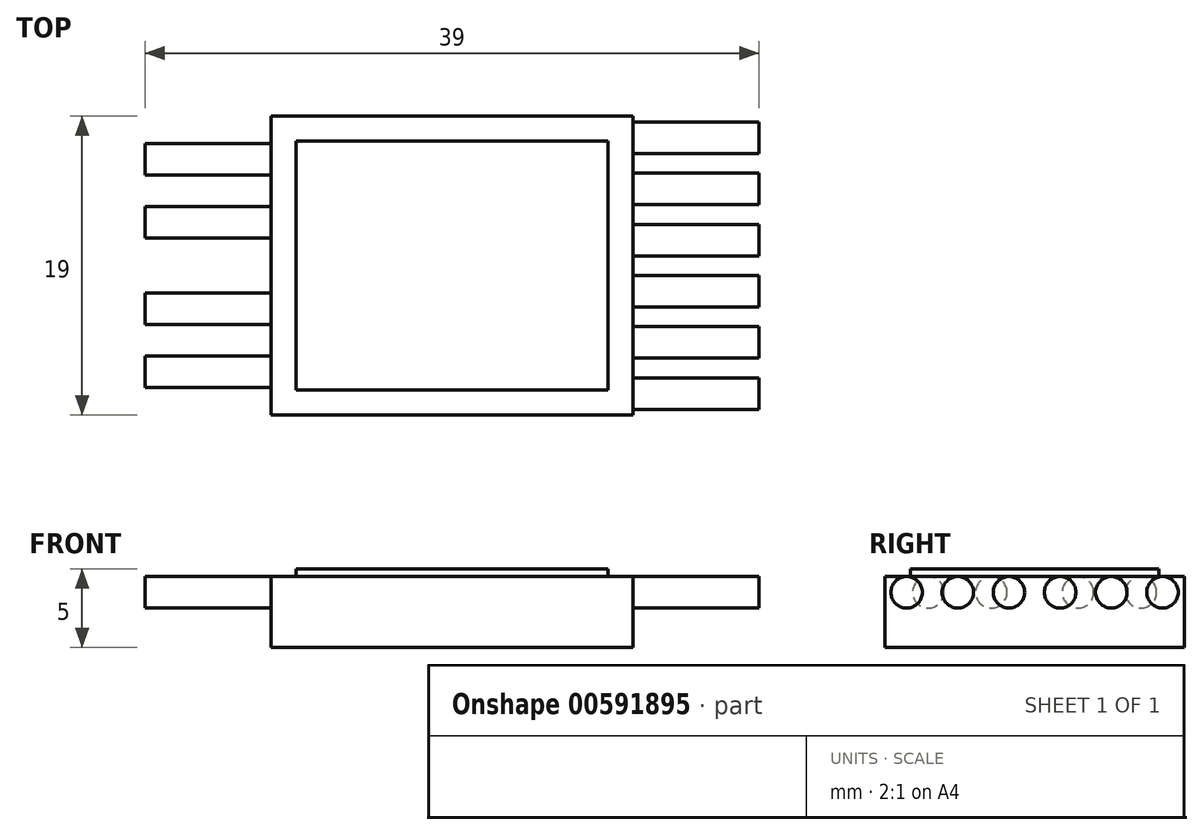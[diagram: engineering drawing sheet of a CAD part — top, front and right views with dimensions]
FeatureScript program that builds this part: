
annotation { "Feature Type Name" : "Feature", "Feature Type Description" : "" }
export const myFeature = defineFeature(function(context is Context, id is Id, definition is map)
    precondition{}
    {
        {
            var Q0;
            Q0=qCreatedBy(makeId("Top.planeOp"),FACE);
            var sketch = newSketch(context, id + "F0", { "sketchPlane" : qUnion([Q0])});
            skLineSegment(sketch, "E0.bottom", {"start": v(11.5, 9.5) * mm, "end": v(-11.5, 9.5) * mm});
            skLineSegment(sketch, "E0.top", {"start": v(11.5, -9.5) * mm, "end": v(-11.5, -9.5) * mm});
            skLineSegment(sketch, "E0.left", {"start": v(11.5, 9.5) * mm, "end": v(11.5, -9.5) * mm});
            skLineSegment(sketch, "E0.right", {"start": v(-11.5, 9.5) * mm, "end": v(-11.5, -9.5) * mm});
            skPoint(sketch, "E0.middle", {"position": v(0, 0) * mm});
            skSolve(sketch);
        }
        {
            var Q0;
            Q0 = qSketchRegion(id + "F0", true);
            extrude(context, id + "F1", {"entities" : qUnion([Q0]), "depth" : 5 * mm, "offsetDistance" : 25 * mm, "symmetric" : true});
        }
        {
            var Q0;
            Q0=makeQuery(id+"F1.opExtrude","SWEPT_FACE",FACE,{"disambiguationData":[OSD([sQuery(id+"F0.wireOp",EDGE,"E0.left")])]});
            var sketch = newSketch(context, id + "F2", { "sketchPlane" : qUnion([Q0])});
            skCircle(sketch, "E1", {"center": v(-8.13, 1) * mm, "radius": 1 * mm});
            skCircle(sketch, "E2.1.0.0", {"center": v(-4.88, 1) * mm, "radius": 1 * mm});
            skCircle(sketch, "E2.2.0.0", {"center": v(-1.63, 1) * mm, "radius": 1 * mm});
            skCircle(sketch, "E2.3.0.0", {"center": v(1.62, 1) * mm, "radius": 1 * mm});
            skCircle(sketch, "E2.4.0.0", {"center": v(4.87, 1) * mm, "radius": 1 * mm});
            skCircle(sketch, "E2.5.0.0", {"center": v(8.12, 1) * mm, "radius": 1 * mm});
            skLineSegment(sketch, "E2.direction1", {"start": v(-8.13, 1) * mm, "end": v(-4.88, 1) * mm, "construction": true});
            skLineSegment(sketch, "E3", {"start": v(-1.63, 1) * mm, "end": v(1.62, 1) * mm, "construction": true});
            skPoint(sketch, "E4", {"position": v(0, 1) * mm});
            skSolve(sketch);
        }
        {
            var Q0;
            Q0 = qSketchRegion(id + "F2", true);
            extrude(context, id + "F3", {"entities" : qUnion([Q0]), "operationType" : NewBodyOperationType.ADD, "depth" : 8 * mm, "offsetDistance" : 25 * mm});
        }
        {
            var Q0;
            Q0=makeQuery(id+"F1.opExtrude","SWEPT_FACE",FACE,{"disambiguationData":[OSD([sQuery(id+"F0.wireOp",EDGE,"E0.right")])]});
            var sketch = newSketch(context, id + "F4", { "sketchPlane" : qUnion([Q0])});
            skCircle(sketch, "E5", {"center": v(-6.75, 1) * mm, "radius": 1 * mm});
            skCircle(sketch, "E6", {"center": v(-2.75, 1) * mm, "radius": 1 * mm});
            skCircle(sketch, "E7", {"center": v(2.75, 1) * mm, "radius": 1 * mm});
            skCircle(sketch, "E8", {"center": v(6.75, 1) * mm, "radius": 1 * mm});
            skLineSegment(sketch, "E9", {"start": v(-6.75, 1) * mm, "end": v(-2.75, 1) * mm, "construction": true});
            skLineSegment(sketch, "E10", {"start": v(2.75, 1) * mm, "end": v(6.75, 1) * mm, "construction": true});
            skLineSegment(sketch, "E11", {"start": v(-2.75, 1) * mm, "end": v(2.75, 1) * mm, "construction": true});
            skPoint(sketch, "E12", {"position": v(0, 1) * mm});
            skSolve(sketch);
        }
        {
            var Q0;
            Q0 = qSketchRegion(id + "F4", true);
            extrude(context, id + "F5", {"entities" : qUnion([Q0]), "operationType" : NewBodyOperationType.ADD, "depth" : 8 * mm, "offsetDistance" : 25 * mm});
        }
        {
            var Q0;
            Q0=makeQuery(id+"F1.opExtrude","CAP_FACE",FACE,{"disambiguationData":[OSD([sQuery(id+"F0.wireOp",EDGE,"E0.bottom"),sQuery(id+"F0.wireOp",EDGE,"E0.top"),sQuery(id+"F0.wireOp",EDGE,"E0.left"),sQuery(id+"F0.wireOp",EDGE,"E0.right")])],"isStart":false});
            var sketch = newSketch(context, id + "F6", { "sketchPlane" : qUnion([Q0])});
            skLineSegment(sketch, "E13.0", {"start": v(9.9, 7.9) * mm, "end": v(-9.9, 7.9) * mm});
            skLineSegment(sketch, "E13.1", {"start": v(9.9, 7.9) * mm, "end": v(9.9, -7.9) * mm});
            skLineSegment(sketch, "E13.2", {"start": v(9.9, -7.9) * mm, "end": v(-9.9, -7.9) * mm});
            skLineSegment(sketch, "E13.3", {"start": v(-9.9, 7.9) * mm, "end": v(-9.9, -7.9) * mm});
            skLineSegment(sketch, "E14.0", {"start": v(11.5, 9.5) * mm, "end": v(-11.5, 9.5) * mm});
            skLineSegment(sketch, "E14.1", {"start": v(-11.5, 9.5) * mm, "end": v(-11.5, -9.5) * mm});
            skLineSegment(sketch, "E14.2", {"start": v(11.5, 9.5) * mm, "end": v(11.5, -9.5) * mm});
            skLineSegment(sketch, "E14.3", {"start": v(11.5, -9.5) * mm, "end": v(-11.5, -9.5) * mm});
            skSolve(sketch);
        }
        {
            var Q0;
            Q0 = qSketchRegion(id + "F6", true);
            extrude(context, id + "F7", {"entities" : qUnion([Q0]), "operationType" : NewBodyOperationType.REMOVE, "oppositeDirection" : true, "depth" : 0.5 * mm, "offsetDistance" : 25 * mm});
        }
    });
